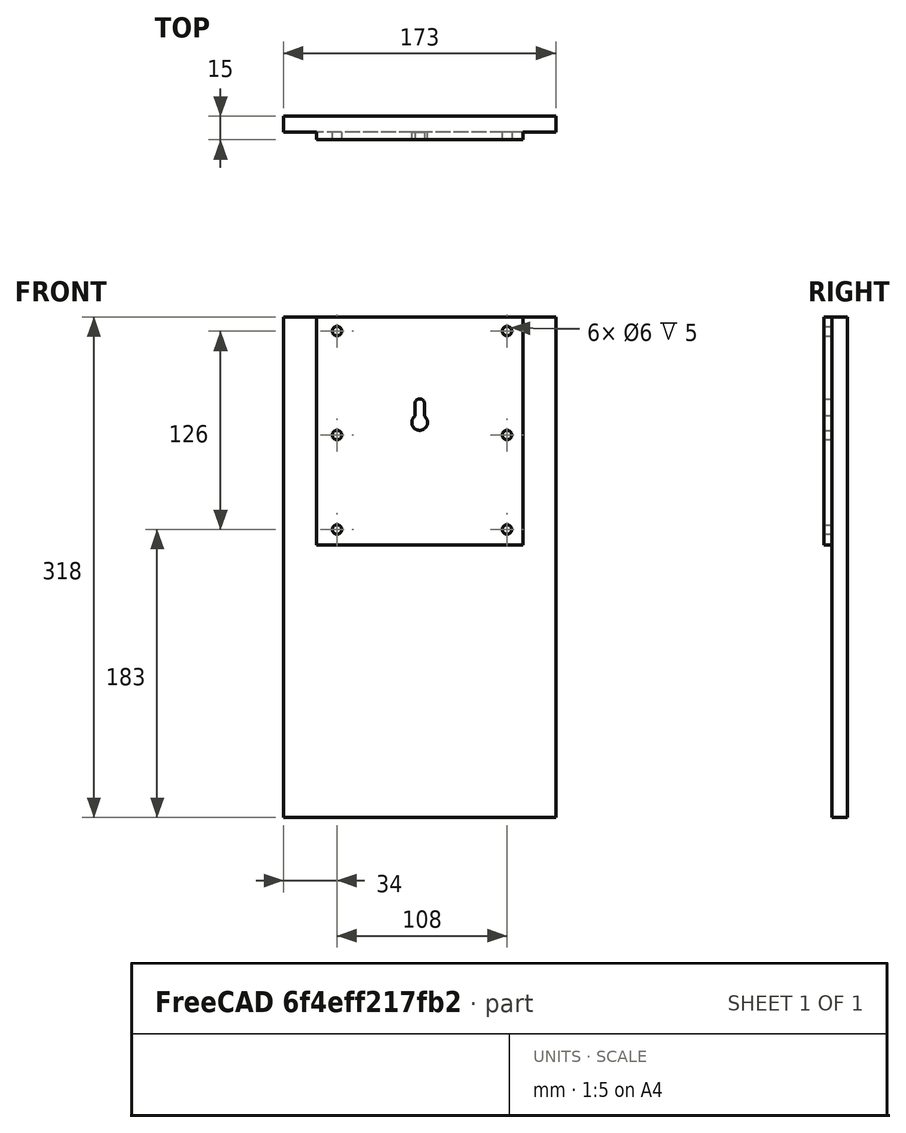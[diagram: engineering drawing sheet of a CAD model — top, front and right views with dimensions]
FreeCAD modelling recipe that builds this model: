
FCSTD DOCUMENT  (FreeCAD 0.20R29177 +426 (Git))
Label: rp500sa
License: All rights reserved
LicenseURL: http://en.wikipedia.org/wiki/All_rights_reserved
objects: TechDraw::DrawViewDimension×6, TechDraw::DrawViewAnnotation×4, Sketcher::SketchObject×3, PartDesign::Pad×2, PartDesign::Pocket×1, PartDesign::Body×1, TechDraw::DrawSVGTemplate×1, TechDraw::DrawViewPart×1, TechDraw::DrawPage×1
note: 10 computed .brp shape members not serialized (recipe doc carries the construction recipe); baked Part::Feature solids carry a one-line shape summary decoded from their .brp

FEATURE [Sketcher::SketchObject] Sketch
  FullyConstrained = true
  MapMode = 5
  Placement = pos=(0,0,0) rot=(1,0,0;1.5708rad)
  Support = -> [XZ_Plane]
  sketch-geometry (4):
    g0: LineSegment StartX=-86.5 StartY=159 StartZ=0 EndX=86.5 EndY=159 EndZ=0
    g1: LineSegment StartX=86.5 StartY=159 StartZ=0 EndX=86.5 EndY=-159 EndZ=0
    g2: LineSegment StartX=86.5 StartY=-159 StartZ=0 EndX=-86.5 EndY=-159 EndZ=0
    g3: LineSegment StartX=-86.5 StartY=-159 StartZ=0 EndX=-86.5 EndY=159 EndZ=0
  constraints (11):
    c: Coincident(g0,g1)
    c: Coincident(g1,g2)
    c: Coincident(g2,g3)
    c: Coincident(g3,g0)
    c: Horizontal(g0)
    c: Horizontal(g2)
    c: Vertical(g1)
    c: Vertical(g3)
    c: Symmetric(g0,g2,g-1)
    c: DistanceX(g0,g0) = 173
    c: DistanceY(g1,g1) = 318
FEATURE [PartDesign::Pad] Pad
  Direction = (0,-1,2e-16)
  Length = 10
  Length2 = 10
  Placement = pos=(0,0,0) rot=(1,0,0;1.5708rad)
  Profile = -> Sketch
  ReferenceAxis = -> Sketch [N_Axis]
  Reversed = true
  Type = 0
FEATURE [Sketcher::SketchObject] Sketch001
  ExternalGeometry = -> [Sketch]
  FullyConstrained = true
  MapMode = 5
  Placement = pos=(0,0,0) rot=(1,0,0;1.5708rad)
  Support = -> [XZ_Plane]
  sketch-geometry (4):
    g0: LineSegment StartX=-65.5 StartY=159 StartZ=0 EndX=65.5 EndY=159 EndZ=0
    g1: LineSegment StartX=65.5 StartY=159 StartZ=0 EndX=65.5 EndY=14 EndZ=0
    g2: LineSegment StartX=65.5 StartY=14 StartZ=0 EndX=-65.5 EndY=14 EndZ=0
    g3: LineSegment StartX=-65.5 StartY=14 StartZ=0 EndX=-65.5 EndY=159 EndZ=0
  constraints (12):
    c: Coincident(g0,g1)
    c: Coincident(g1,g2)
    c: Coincident(g2,g3)
    c: Coincident(g3,g0)
    c: Horizontal(g0)
    c: Horizontal(g2)
    c: Vertical(g1)
    c: Vertical(g3)
    c: DistanceY(g0,g-4) = 0
    c: DistanceY(g3,g3) = 145
    c: DistanceX(g0,g-6) = 21
    c: DistanceX(g-4,g0) = 21
FEATURE [PartDesign::Pad] Pad001
  BaseFeature = -> Pad
  Direction = (0,-1,-2e-16)
  Length = 5
  Length2 = 10
  Placement = pos=(0,0,0) rot=(1,0,0;1.5708rad)
  Profile = -> Sketch001
  ReferenceAxis = -> Sketch001 [N_Axis]
  Type = 0
FEATURE [Sketcher::SketchObject] Sketch002
  ExternalGeometry = -> [Sketch001]
  FullyConstrained = false
  MapMode = 5
  Placement = pos=(0,0,0) rot=(1,0,0;1.5708rad)
  Support = -> [XZ_Plane]
  sketch-geometry (42):
    g0: Circle CenterX=-52.5 CenterY=150 CenterZ=0 NormalX=0 NormalY=0 NormalZ=1 AngleXU=0 Radius=3
    g1: LineSegment StartX=-55.5 StartY=153 StartZ=0 EndX=-49.5 EndY=153 EndZ=0
    g2: LineSegment StartX=-49.5 StartY=153 StartZ=0 EndX=-49.5 EndY=147 EndZ=0
    g3: LineSegment StartX=-49.5 StartY=147 StartZ=0 EndX=-55.5 EndY=147 EndZ=0
    g4: LineSegment StartX=-55.5 StartY=147 StartZ=0 EndX=-55.5 EndY=153 EndZ=0
    g5: Circle CenterX=-52.5 CenterY=84 CenterZ=0 NormalX=0 NormalY=0 NormalZ=1 AngleXU=0 Radius=3
    g6: LineSegment StartX=-49.5 StartY=81 StartZ=0 EndX=-55.5 EndY=81 EndZ=0
    g7: LineSegment StartX=-55.5 StartY=81 StartZ=0 EndX=-55.5 EndY=87 EndZ=0
    g8: LineSegment StartX=-55.5 StartY=87 StartZ=0 EndX=-49.5 EndY=87 EndZ=0
    g9: LineSegment StartX=-49.5 StartY=87 StartZ=0 EndX=-49.5 EndY=81 EndZ=0
    g10: Circle CenterX=-52.5 CenterY=24 CenterZ=0 NormalX=0 NormalY=0 NormalZ=1 AngleXU=0 Radius=3
    g11: LineSegment StartX=-55.5 StartY=21 StartZ=0 EndX=-49.5 EndY=21 EndZ=0
    g12: LineSegment StartX=-49.5 StartY=21 StartZ=0 EndX=-49.5 EndY=27 EndZ=0
    g13: LineSegment StartX=-49.5 StartY=27 StartZ=0 EndX=-55.5 EndY=27 EndZ=0
    g14: LineSegment StartX=-55.5 StartY=27 StartZ=0 EndX=-55.5 EndY=21 EndZ=0
    g15: Circle CenterX=55.5 CenterY=150 CenterZ=0 NormalX=0 NormalY=0 NormalZ=1 AngleXU=0 Radius=3
    g16: LineSegment StartX=52.5 StartY=153 StartZ=0 EndX=58.5 EndY=153 EndZ=0
    g17: LineSegment StartX=58.5 StartY=153 StartZ=0 EndX=58.5 EndY=147 EndZ=0
    g18: LineSegment StartX=58.5 StartY=147 StartZ=0 EndX=52.5 EndY=147 EndZ=0
    g19: LineSegment StartX=52.5 StartY=147 StartZ=0 EndX=52.5 EndY=153 EndZ=0
    g20: Circle CenterX=55.5 CenterY=84 CenterZ=0 NormalX=0 NormalY=0 NormalZ=1 AngleXU=0 Radius=3
    g21: LineSegment StartX=52.5 StartY=81 StartZ=0 EndX=58.5 EndY=81 EndZ=0
    g22: LineSegment StartX=58.5 StartY=81 StartZ=0 EndX=58.5 EndY=87 EndZ=0
    g23: LineSegment StartX=58.5 StartY=87 StartZ=0 EndX=52.5 EndY=87 EndZ=0
    g24: LineSegment StartX=52.5 StartY=87 StartZ=0 EndX=52.5 EndY=81 EndZ=0
    g25: Circle CenterX=55.5 CenterY=24 CenterZ=0 NormalX=0 NormalY=0 NormalZ=1 AngleXU=0 Radius=3
    g26: LineSegment StartX=52.5 StartY=21 StartZ=0 EndX=58.5 EndY=21 EndZ=0
    g27: LineSegment StartX=58.5 StartY=21 StartZ=0 EndX=58.5 EndY=27 EndZ=0
    g28: LineSegment StartX=58.5 StartY=27 StartZ=0 EndX=52.5 EndY=27 EndZ=0
    g29: LineSegment StartX=52.5 StartY=27 StartZ=0 EndX=52.5 EndY=21 EndZ=0
    g30: ArcOfCircle CenterX=0 CenterY=104 CenterZ=0 NormalX=0 NormalY=0 NormalZ=1 AngleXU=0 Radius=3 StartAngle=0 EndAngle=3.14159
    g31: LineSegment StartX=3 StartY=107 StartZ=0 EndX=-3 EndY=107 EndZ=0
    g32: LineSegment StartX=-3 StartY=107 StartZ=0 EndX=-3 EndY=101 EndZ=0
    g33: LineSegment StartX=-3 StartY=101 StartZ=0 EndX=3 EndY=101 EndZ=0
    g34: LineSegment StartX=3 StartY=101 StartZ=0 EndX=3 EndY=107 EndZ=0
    g35: ArcOfCircle CenterX=0 CenterY=92 CenterZ=0 NormalX=0 NormalY=0 NormalZ=1 AngleXU=0 Radius=5 StartAngle=2.2143 EndAngle=7.21048
    g36: LineSegment StartX=-5 StartY=97 StartZ=0 EndX=5 EndY=97 EndZ=0
    g37: LineSegment StartX=5 StartY=97 StartZ=0 EndX=5 EndY=87 EndZ=0
    g38: LineSegment StartX=5 StartY=87 StartZ=0 EndX=-5 EndY=87 EndZ=0
    g39: LineSegment StartX=-5 StartY=87 StartZ=0 EndX=-5 EndY=97 EndZ=0
    g40: LineSegment StartX=-3 StartY=104 StartZ=0 EndX=-3 EndY=96 EndZ=0
    g41: LineSegment StartX=3 StartY=104 StartZ=0 EndX=3 EndY=96 EndZ=0
  constraints (117):
    c: Diameter(g0) = 6
    c: Coincident(g1,g2)
    c: Coincident(g2,g3)
    c: Coincident(g3,g4)
    c: Coincident(g4,g1)
    c: Horizontal(g1)
    c: Horizontal(g3)
    c: Vertical(g2)
    c: Vertical(g4)
    c: Equal(g1,g4)
    c: Symmetric(g1,g3,g0)
    c: Tangent(g0,g3)
    c: DistanceX(g-4,g3) = 10
    c: DistanceY(g0,g-4) = 9
    c: Equal(g0,g5) = 6
    c: Coincident(g6,g7)
    c: Coincident(g7,g8)
    c: Coincident(g8,g9)
    c: Coincident(g9,g6)
    c: Horizontal(g6)
    c: Horizontal(g8)
    c: Vertical(g7)
    c: Vertical(g9)
    c: Equal(g6,g9)
    c: Symmetric(g6,g8,g5)
    c: Tangent(g5,g8)
    c: DistanceY(g5,g-4) = 75
    c: DistanceX(g-4,g7) = 10
    c: Coincident(g11,g12)
    c: Coincident(g12,g13)
    c: Coincident(g13,g14)
    c: Coincident(g14,g11)
    c: Horizontal(g11)
    c: Horizontal(g13)
    c: Vertical(g12)
    c: Vertical(g14)
    c: Equal(g11,g14)
    c: Symmetric(g11,g13,g10)
    c: Tangent(g10,g13)
    c: DistanceY(g10,g-4) = 135
    c: Diameter(g10) = 6
    c: DistanceX(g-5,g13) = 10
    c: Coincident(g16,g17)
    c: Coincident(g17,g18)
    c: Coincident(g18,g19)
    c: Coincident(g19,g16)
    c: Horizontal(g16)
    c: Horizontal(g18)
    c: Vertical(g17)
    c: Vertical(g19)
    c: Equal(g16,g19)
    c: Symmetric(g16,g18,g15)
    c: Tangent(g15,g18)
    c: Equal(g10,g15) = 6
    c: Coincident(g21,g22)
    c: Coincident(g22,g23)
    c: Coincident(g23,g24)
    c: Coincident(g24,g21)
    c: Horizontal(g21)
    c: Horizontal(g23)
    c: Vertical(g22)
    c: Vertical(g24)
    c: Equal(g21,g24)
    c: Symmetric(g21,g23,g20)
    c: Tangent(g20,g23)
    c: Equal(g10,g20) = 6
    c: Coincident(g26,g27)
    c: Coincident(g27,g28)
    c: Coincident(g28,g29)
    c: Coincident(g29,g26)
    c: Horizontal(g26)
    c: Horizontal(g28)
    c: Vertical(g27)
    c: Vertical(g29)
    c: Equal(g26,g29)
    c: Symmetric(g26,g28,g25)
    c: Tangent(g25,g28)
    c: Equal(g10,g25) = 6
    c: DistanceY(g15,g-6) = 9
    c: DistanceY(g20,g-6) = 75
    c: DistanceY(g25,g-6) = 135
    c: DistanceX(g15,g-6) = 10
    c: DistanceX(g20,g-6) = 10
    c: DistanceX(g25,g-6) = 10
    c: Coincident(g31,g32)
    c: Coincident(g32,g33)
    c: Coincident(g33,g34)
    c: Coincident(g34,g31)
    c: Horizontal(g31)
    c: Horizontal(g33)
    c: Vertical(g32)
    c: Vertical(g34)
    c: Equal(g31,g34)
    c: Symmetric(g31,g33,g30)
    c: PointOnObject(g30,g-2)
    c: Diameter(g30) = 6
    c: DistanceY(g31,g-6) = 52
    c: Diameter(g35) = 10
    c: PointOnObject(g35,g-2)
    c: Coincident(g36,g37)
    c: Coincident(g37,g38)
    c: Coincident(g38,g39)
    c: Coincident(g39,g36)
    c: Horizontal(g36)
    c: Horizontal(g38)
    c: Vertical(g37)
    c: Vertical(g39)
    c: Equal(g39,g36)
    c: Symmetric(g36,g38,g35)
    c: Vertical(g40)
    c: Vertical(g41)
    c: DistanceY(g37,g31) = 20
    c: Tangent(g40,g30) = -1.5708
    c: Tangent(g41,g30) = 1.5708
    c: Coincident(g35,g41)
    c: Coincident(g35,g40)
    c: PointOnObject(g30,g34)
FEATURE [PartDesign::Pocket] Pocket
  BaseFeature = -> Pad001
  Direction = (0,1,2e-16)
  Length = 5
  Length2 = 5
  Placement = pos=(0,0,0) rot=(1,0,0;1.5708rad)
  Profile = -> Sketch002
  ReferenceAxis = -> Sketch002 [N_Axis]
  Reversed = true
  Type = 0
FEATURE [PartDesign::Body] Body
  Group = -> [Sketch,Pad,Sketch001,Pad001,Sketch002,Pocket]
  Origin = -> Origin
  Tip = -> Pocket
FEATURE [TechDraw::DrawSVGTemplate] Template002
  Height = 420
  Orientation = 0
  Width = 297
FEATURE [TechDraw::DrawViewPart] View002
  CoarseView = false
  Direction = (0,-1,0)
  Focus = 100
  HardHidden = false
  IsoCount = 0
  IsoHidden = false
  IsoVisible = false
  LockPosition = false
  Perspective = false
  Rotation = 0
  ScaleType = 0
  SeamHidden = false
  SeamVisible = true
  SmoothHidden = false
  SmoothVisible = true
  Source = -> [Pocket]
  X = 148.5
  XDirection = (1,0,0)
  Y = 210
FEATURE [TechDraw::DrawViewDimension] Dimension010
  AngleOverride = false
  Arbitrary = false
  ArbitraryTolerances = false
  EqualTolerance = true
  ExtensionAngle = 0
  FormatSpec = ⌀%.2w
  FormatSpecOverTolerance = %+.2w
  FormatSpecUnderTolerance = %+.2w
  Inverted = false
  LineAngle = 0
  LockPosition = false
  MeasureType = 1
  OverTolerance = 0
  References2D = -> [View002]
  Rotation = 0
  ScaleType = 0
  TheoreticalExact = false
  Type = 5
  UnderTolerance = 0
  X = 19.0952
  Y = 127.226
FEATURE [TechDraw::DrawViewDimension] Dimension011
  AngleOverride = false
  Arbitrary = false
  ArbitraryTolerances = false
  EqualTolerance = true
  ExtensionAngle = 0
  FormatSpec = %.2w
  FormatSpecOverTolerance = %+.2w
  FormatSpecUnderTolerance = %+.2w
  Inverted = false
  LineAngle = 0
  LockPosition = false
  MeasureType = 1
  OverTolerance = 0
  References2D = -> [View002]
  Rotation = 0
  ScaleType = 0
  TheoreticalExact = false
  Type = 2
  UnderTolerance = 0
  X = -32.8963
  Y = 128.496
FEATURE [TechDraw::DrawViewDimension] Dimension012
  AngleOverride = false
  Arbitrary = false
  ArbitraryTolerances = false
  EqualTolerance = true
  ExtensionAngle = 0
  FormatSpec = %.2w
  FormatSpecOverTolerance = %+.2w
  FormatSpecUnderTolerance = %+.2w
  Inverted = false
  LineAngle = 0
  LockPosition = false
  MeasureType = 1
  OverTolerance = 0
  References2D = -> [View002]
  Rotation = 0
  ScaleType = 0
  TheoreticalExact = false
  Type = 1
  UnderTolerance = 0
  X = 38.0278
  Y = 105.863
FEATURE [TechDraw::DrawViewAnnotation] Annotation002
  Font = osifont
  LineSpace = 80
  LockPosition = false
  MaxWidth = -1
  Rotation = 0
  ScaleType = 0
  Text = KEYHOLE SLOT
  TextSize = 5
  TextStyle = 0
  X = 149.519
  Y = 290.989
FEATURE [TechDraw::DrawViewDimension] Dimension014
  AngleOverride = false
  Arbitrary = false
  ArbitraryTolerances = false
  EqualTolerance = true
  ExtensionAngle = 0
  FormatSpec = %.2w
  FormatSpecOverTolerance = %+.2w
  FormatSpecUnderTolerance = %+.2w
  Inverted = false
  LineAngle = 0
  LockPosition = false
  MeasureType = 1
  OverTolerance = 0
  References2D = -> [View002]
  Rotation = 0
  ScaleType = 0
  TheoreticalExact = false
  Type = 1
  UnderTolerance = 0
  X = 0.305618
  Y = 177.086
FEATURE [TechDraw::DrawViewDimension] Dimension015
  AngleOverride = false
  Arbitrary = false
  ArbitraryTolerances = false
  EqualTolerance = true
  ExtensionAngle = 0
  FormatSpec = %.2w
  FormatSpecOverTolerance = %+.2w
  FormatSpecUnderTolerance = %+.2w
  Inverted = false
  LineAngle = 0
  LockPosition = false
  MeasureType = 1
  OverTolerance = 0
  References2D = -> [View002]
  Rotation = 0
  ScaleType = 0
  TheoreticalExact = false
  Type = 2
  UnderTolerance = 0
  X = -105.424
  Y = 3.38018
FEATURE [TechDraw::DrawViewAnnotation] Annotation003
  Font = osifont
  LineSpace = 80
  LockPosition = false
  MaxWidth = -1
  Rotation = 0
  ScaleType = 0
  Text = CENTER OF SPEAKER
  TextSize = 5
  TextStyle = 0
  X = 171.749
  Y = 211.395
FEATURE [TechDraw::DrawViewAnnotation] Annotation004
  Font = Arial
  LineSpace = 80
  LockPosition = false
  MaxWidth = -1
  Rotation = 0
  ScaleType = 0
  Text = Klipsch RP-500SA
  TextSize = 10
  TextStyle = 0
  X = 71.3655
  Y = 401.192
FEATURE [TechDraw::DrawViewAnnotation] Annotation005
  Font = Arial
  LineSpace = 80
  LockPosition = false
  MaxWidth = -1
  Rotation = 0
  ScaleType = 0
  Text = Wall Mounting Template
  TextSize = 7
  TextStyle = 0
  X = 67.6517
  Y = 391.278
FEATURE [TechDraw::DrawViewDimension] Dimension016
  AngleOverride = false
  Arbitrary = false
  ArbitraryTolerances = false
  EqualTolerance = true
  ExtensionAngle = 0
  FormatSpec = %.2w
  FormatSpecOverTolerance = %+.2w
  FormatSpecUnderTolerance = %+.2w
  Inverted = false
  LineAngle = 0
  LockPosition = false
  MeasureType = 1
  OverTolerance = 0
  References2D = -> [View002]
  Rotation = 0
  ScaleType = 0
  TheoreticalExact = false
  Type = 1
  UnderTolerance = 0
  X = -45.7326
  Y = 106.009
FEATURE [TechDraw::DrawPage] Page002
  KeepUpdated = true
  NextBalloonIndex = 1
  ProjectionType = 0
  Template = -> Template002
  Views = -> [View002,Dimension010,Dimension011,Dimension012,Annotation002,Dimension014,Dimension015,Annotation003,Annotation004,Annotation005,Dimension016]
